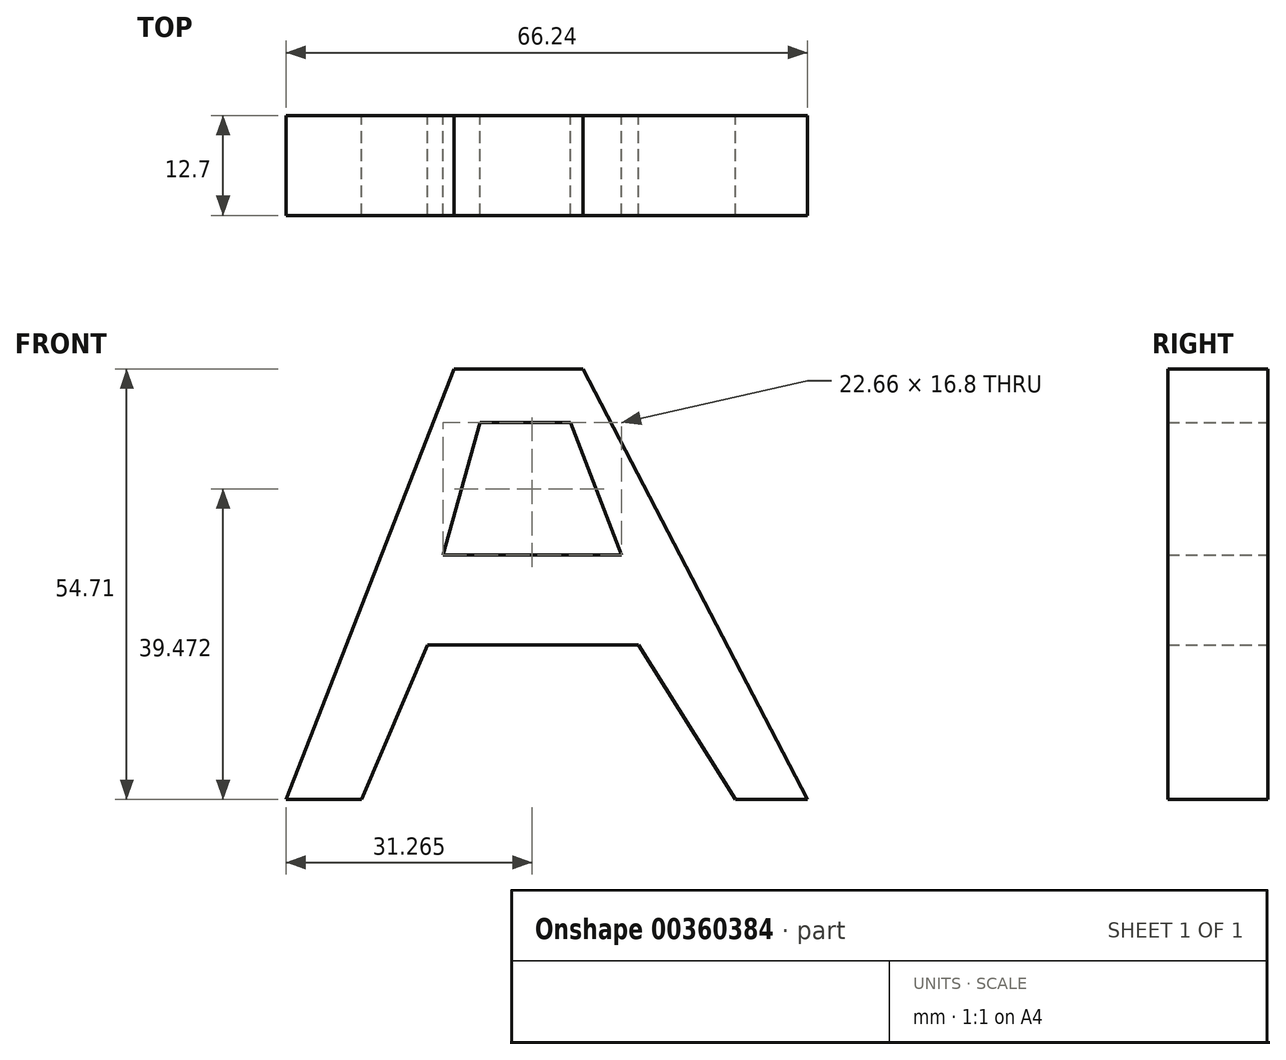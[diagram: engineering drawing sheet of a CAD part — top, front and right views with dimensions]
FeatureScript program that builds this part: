
annotation { "Feature Type Name" : "Feature", "Feature Type Description" : "" }
export const myFeature = defineFeature(function(context is Context, id is Id, definition is map)
    precondition{}
    {
        {
            var Q0;
            Q0=qCreatedBy(makeId("Front.planeOp"),FACE);
            var sketch = newSketch(context, id + "F0", { "sketchPlane" : qUnion([Q0])});
            skLineSegment(sketch, "E0", {"start": v(-8.5, 35.07) * mm, "end": v(7.91, 35.07) * mm});
            skLineSegment(sketch, "E1", {"start": v(7.91, 35.07) * mm, "end": v(36.44, -19.64) * mm});
            skLineSegment(sketch, "E2", {"start": v(36.44, -19.64) * mm, "end": v(27.26, -19.64) * mm});
            skLineSegment(sketch, "E3", {"start": v(27.26, -19.64) * mm, "end": v(14.95, 0) * mm});
            skLineSegment(sketch, "E4", {"start": v(14.95, 0) * mm, "end": v(-11.82, 0) * mm});
            skLineSegment(sketch, "E5", {"start": v(-11.82, 0) * mm, "end": v(-20.22, -19.64) * mm});
            skLineSegment(sketch, "E6", {"start": v(-20.22, -19.64) * mm, "end": v(-29.8, -19.64) * mm});
            skLineSegment(sketch, "E7", {"start": v(-29.8, -19.64) * mm, "end": v(-8.5, 35.07) * mm});
            skLineSegment(sketch, "E8", {"start": v(-5.18, 28.23) * mm, "end": v(6.35, 28.23) * mm});
            skLineSegment(sketch, "E9", {"start": v(6.35, 28.23) * mm, "end": v(12.8, 11.43) * mm});
            skLineSegment(sketch, "E10", {"start": v(12.8, 11.43) * mm, "end": v(-9.87, 11.43) * mm});
            skLineSegment(sketch, "E11", {"start": v(-9.87, 11.43) * mm, "end": v(-5.18, 28.23) * mm});
            skSolve(sketch);
        }
        {
            var Q0;
            Q0=makeQuery(id+"F0.imprint","IMPRINT",FACE,{"disambiguationData":[TD([[makeQuery(id+"F0.imprint","IMPRINT",EDGE,{"derivedFrom":sQuery(id+"F0.wireOp",EDGE,"E0")}),-1.0]])]});
            extrude(context, id + "F1", {"entities" : qUnion([Q0]), "depth" : 12.7 * mm});
        }
    });
